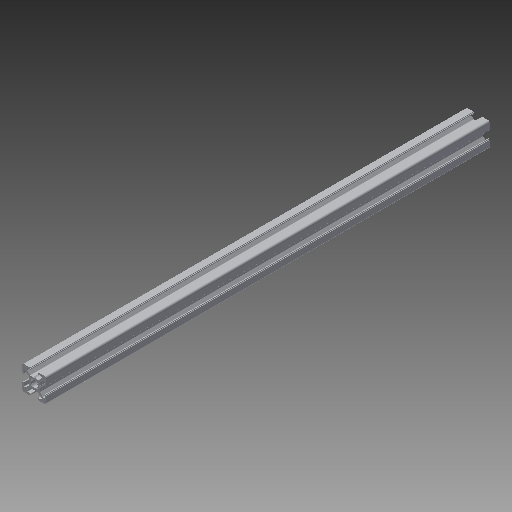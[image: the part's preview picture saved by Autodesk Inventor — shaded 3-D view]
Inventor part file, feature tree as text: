
AUTODESK INVENTOR PART (.ipt)
format: ipt  version: 2017 (Build 210142000, 142)  size: 314,368 bytes
history: native  units: in
note: dims shown in document units (in); Inventor stores cm internally (conversion verified against a paired STEP export)
features: other x3, extrude x1, sketch x1
ambient origin geometry x8: Origin, YZ Plane, XZ Plane, XY Plane, X Axis, Y Axis, Z Axis, Center Point
bodies: Solid1 (feature_tree)
feature tree (5):
  other  "Blocks"
  extrude  "Extrusion1"  [1 undecoded]
  sketch  "Sketch1"  dims[d1=0.0in]
  other  "20x20"
  other  "20x20:1"
note: 1 required parameter value undecoded (feature->parameter linkage not recoverable at this tier; creation-order binding heuristic only, values carry confidence <= 0.55)
